FCSTD DOCUMENT  (FreeCAD 1.0R39319 (Git))
Label: assembly main
License: All rights reserved
LicenseURL: https://en.wikipedia.org/wiki/All_rights_reserved
objects: App::Link×10, App::FeaturePython×8, Assembly::AssemblyLink×2, Assembly::JointGroup×1, Assembly::AssemblyObject×1
EXTERNAL_REF file=Sub-Assembly.FCStd obj=Assembly
EXTERNAL_REF file=Sub-Assembly.FCStd obj=Base
EXTERNAL_REF file=Sub-Assembly.FCStd obj=Bracket
EXTERNAL_REF file=Sub-Assembly.FCStd obj=Bracket001
EXTERNAL_REF file=Base-Bracket.FCStd obj=Body002

FEATURE [App::Link] Base
  LinkedObject = -> <external Sub-Assembly.FCStd>#Base
FEATURE [App::Link] Bracket
  LinkPlacement = pos=(-27.5,-2.2e-15,10) rot=(0,0,1;1.5708rad)
  LinkedObject = -> <external Sub-Assembly.FCStd>#Bracket
  Placement = pos=(-27.5,-2.2e-15,10) rot=(0,0,1;1.5708rad)
FEATURE [App::Link] Bracket001
  LinkPlacement = pos=(27.5,-4.7e-15,10) rot=(0,0,-1;1.5708rad)
  LinkedObject = -> <external Sub-Assembly.FCStd>#Bracket001
  Placement = pos=(27.5,-4.7e-15,10) rot=(0,0,-1;1.5708rad)
FEATURE [Assembly::AssemblyLink] Assembly001
  Group = -> [Base,Bracket,Bracket001]
  LinkedObject = -> <external Sub-Assembly.FCStd>#Assembly
  Origin = -> Origin001
  Rigid = true
FEATURE [App::FeaturePython] GroundedJoint  # Assembly grounded joint (typed FeaturePython)
  ObjectToGround = -> Assembly001
FEATURE [App::Link] Base001
  LinkedObject = -> <external Sub-Assembly.FCStd>#Base
FEATURE [App::Link] Bracket002
  LinkPlacement = pos=(-27.5,-2.2e-15,10) rot=(0,0,1;1.5708rad)
  LinkedObject = -> <external Sub-Assembly.FCStd>#Bracket
  Placement = pos=(-27.5,-2.2e-15,10) rot=(0,0,1;1.5708rad)
FEATURE [App::Link] Bracket003
  LinkPlacement = pos=(27.5,-4.7e-15,10) rot=(0,0,-1;1.5708rad)
  LinkedObject = -> <external Sub-Assembly.FCStd>#Bracket001
  Placement = pos=(27.5,-4.7e-15,10) rot=(0,0,-1;1.5708rad)
FEATURE [Assembly::AssemblyLink] Assembly002
  Group = -> [Base001,Bracket002,Bracket003]
  LinkedObject = -> <external Sub-Assembly.FCStd>#Assembly
  Origin = -> Origin002
  Placement = pos=(-5e-16,111.569,4.2e-15) rot=(0,0,1;0rad)
  Rigid = true
FEATURE [App::FeaturePython] Joint  label="Slider"  # Assembly joint (typed FeaturePython)
  Activated = true
  AngleMax = 0
  AngleMin = 0
  Detach1 = false
  Detach2 = false
  Distance = 0
  Distance2 = 0
  EnableAngleMax = false
  EnableAngleMin = false
  EnableLengthMax = true
  EnableLengthMin = true
  JointType = 3 (Slider)
  LengthMax = 180
  LengthMin = 70
  Placement1 = pos=(-27.5,0,10) rot=(-0.57735,-0.57735,0.57735;4.18879rad)
  Placement2 = pos=(-27.5,0,10) rot=(-0.57735,-0.57735,0.57735;4.18879rad)
  Reference1 = -> Assembly [Assembly002.Base001.Edge21,Assembly002.Base001.Edge21]
  Reference2 = -> Assembly [Assembly001.Base.Edge21,Assembly001.Base.Edge21]
FEATURE [App::Link] Link
  LinkPlacement = pos=(25.5,27.8923,101.497) rot=(0.425501,0.798686,0.425501;1.79371rad)
  LinkedObject = -> <external Base-Bracket.FCStd>#Body002
  Placement = pos=(25.5,27.8923,101.497) rot=(0.425501,0.798686,0.425501;1.79371rad)
FEATURE [App::Link] Link001
  LinkPlacement = pos=(-25.5,27.8923,101.497) rot=(-0.425501,0.798686,0.425501;4.48947rad)
  LinkedObject = -> <external Base-Bracket.FCStd>#Body002
  Placement = pos=(-25.5,27.8923,101.497) rot=(-0.425501,0.798686,0.425501;4.48947rad)
FEATURE [App::Link] Link002
  LinkPlacement = pos=(25.5,83.677,101.497) rot=(0.661712,0.352528,0.661712;2.46374rad)
  LinkedObject = -> <external Base-Bracket.FCStd>#Body002
  Placement = pos=(25.5,83.677,101.497) rot=(0.661712,0.352528,0.661712;2.46374rad)
FEATURE [App::Link] Link003
  LinkPlacement = pos=(-25.5,83.677,101.497) rot=(0.425501,0.798686,-0.425501;4.48947rad)
  LinkedObject = -> <external Base-Bracket.FCStd>#Body002
  Placement = pos=(-25.5,83.677,101.497) rot=(0.425501,0.798686,-0.425501;4.48947rad)
FEATURE [App::FeaturePython] Joint001  label="Revolute"  # Assembly joint (typed FeaturePython)
  Activated = true
  AngleMax = 0
  AngleMin = 0
  Detach1 = false
  Detach2 = false
  Distance = 0
  Distance2 = 0
  EnableAngleMax = false
  EnableAngleMin = false
  EnableLengthMax = false
  EnableLengthMin = false
  JointType = 1 (Revolute)
  LengthMax = 0
  LengthMin = 0
  Placement1 = pos=(2.1316e-12,-50,2) rot=(0,0,1;0rad)
  Placement2 = pos=(0,0,50) rot=(1,0,0;1.5708rad)
  Reference1 = -> Assembly [Link002.Pad003.Edge15,Link002.Pad003.Edge15]
  Reference2 = -> Assembly [Assembly002.Bracket003.Pad002.Edge37,Assembly002.Bracket003.Pad002.Edge37]
FEATURE [App::FeaturePython] Joint002  label="Revolute001"  # Assembly joint (typed FeaturePython)
  Activated = true
  AngleMax = 0
  AngleMin = 0
  Detach1 = false
  Detach2 = false
  Distance = 0
  Distance2 = 0
  EnableAngleMax = false
  EnableAngleMin = false
  EnableLengthMax = false
  EnableLengthMin = false
  JointType = 1 (Revolute)
  LengthMax = 0
  LengthMin = 0
  Offset2 = pos=(0,0,5) rot=(0,0,1;0rad)
  Placement1 = pos=(2.1316e-12,50,2) rot=(0,0,1;0rad)
  Placement2 = pos=(-3e-16,-9e-16,50) rot=(1,0,0;1.5708rad)
  Reference1 = -> Assembly [Link003.Pad003.Edge18,Link003.Pad003.Edge18]
  Reference2 = -> Assembly [Assembly002.Bracket002.Pad002.Edge32,Assembly002.Bracket002.Pad002.Edge32]
FEATURE [App::FeaturePython] Joint003  label="Revolute002"  # Assembly joint (typed FeaturePython)
  Activated = true
  AngleMax = 0
  AngleMin = 0
  Detach1 = false
  Detach2 = false
  Distance = 0
  Distance2 = 0
  EnableAngleMax = false
  EnableAngleMin = false
  EnableLengthMax = false
  EnableLengthMin = false
  JointType = 1 (Revolute)
  LengthMax = 0
  LengthMin = 0
  Placement1 = pos=(2.1316e-12,-50,2) rot=(0,0,1;0rad)
  Placement2 = pos=(0,0,50) rot=(1,0,0;1.5708rad)
  Reference1 = -> Assembly [Link.Pad003.Edge15,Link.Pad003.Edge15]
  Reference2 = -> Assembly [Assembly001.Bracket001.Pad002.Edge37,Assembly001.Bracket001.Pad002.Edge37]
FEATURE [App::FeaturePython] Joint004  label="Revolute003"  # Assembly joint (typed FeaturePython)
  Activated = true
  AngleMax = 0
  AngleMin = 0
  Detach1 = false
  Detach2 = false
  Distance = 0
  Distance2 = 0
  EnableAngleMax = false
  EnableAngleMin = false
  EnableLengthMax = false
  EnableLengthMin = false
  JointType = 1 (Revolute)
  LengthMax = 0
  LengthMin = 0
  Placement1 = pos=(2.1316e-12,-50,2) rot=(0,0,1;0rad)
  Placement2 = pos=(0,0,50) rot=(1,0,0;1.5708rad)
  Reference1 = -> Assembly [Link001.Pad003.Edge15,Link001.Pad003.Edge15]
  Reference2 = -> Assembly [Assembly001.Bracket.Pad002.Edge37,Assembly001.Bracket.Pad002.Edge37]
FEATURE [App::FeaturePython] Joint005  label="Revolute004"  # Assembly joint (typed FeaturePython)
  Activated = true
  AngleMax = 0
  AngleMin = 0
  Detach1 = false
  Detach2 = false
  Distance = 0
  Distance2 = 0
  EnableAngleMax = false
  EnableAngleMin = false
  EnableLengthMax = false
  EnableLengthMin = false
  JointType = 1 (Revolute)
  LengthMax = 0
  LengthMin = 0
  Placement1 = pos=(2.1316e-12,-50,1) rot=(0,0,1;0rad)
  Placement2 = pos=(2.1316e-12,50,1) rot=(0,0,1;0rad)
  Reference1 = -> Assembly [Link003.Pad003.Face5,Link003.Pad003.Face5]
  Reference2 = -> Assembly [Link001.Pad003.Face6,Link001.Pad003.Face6]
FEATURE [App::FeaturePython] Joint006  label="Revolute005"  # Assembly joint (typed FeaturePython)
  Activated = true
  AngleMax = 0
  AngleMin = 0
  Detach1 = false
  Detach2 = false
  Distance = 0
  Distance2 = 0
  EnableAngleMax = false
  EnableAngleMin = false
  EnableLengthMax = false
  EnableLengthMin = false
  JointType = 1 (Revolute)
  LengthMax = 0
  LengthMin = 0
  Placement1 = pos=(2.1174e-12,50,1) rot=(0,0,1;0rad)
  Placement2 = pos=(2.1174e-12,50,1) rot=(0,0,1;0rad)
  Reference1 = -> Assembly [Link002.Pad003.Face6,Link002.Pad003.Face6]
  Reference2 = -> Assembly [Link.Pad003.Face6,Link.Pad003.Face6]
FEATURE [Assembly::JointGroup] Joints
  Group = -> [GroundedJoint,Joint,Joint001,Joint002,Joint003,Joint004,Joint005,Joint006]
FEATURE [Assembly::AssemblyObject] Assembly
  Group = -> [Joints,Assembly001,GroundedJoint,Assembly002,Joint,Link,Link001,Link002,Link003,Joint001,Joint002,Joint003,Joint004,Joint005,Joint006]
  Origin = -> Origin
  Type = Assembly

RESOLVED EXTERNAL PARTS (link-assembly join: the EXTERNAL_REF files above that resolve inside this repo's crawl, each included once):
---- part Base-Bracket.FCStd = doc fcstd_38e4ad80bfca ----
FCSTD DOCUMENT  (FreeCAD 1.0R39319 (Git))
Label: Base-Bracket
License: All rights reserved
LicenseURL: https://en.wikipedia.org/wiki/All_rights_reserved
objects: Sketcher::SketchObject×5, PartDesign::Pad×4, PartDesign::Body×3, PartDesign::Pocket×1
note: 28 computed .brp shape members not serialized (recipe doc carries the construction recipe); baked Part::Feature solids carry a one-line shape summary decoded from their .brp

FEATURE [Sketcher::SketchObject] Sketch
  ArcFitTolerance = 1e-06
  AttachmentSupport = -> [XY_Plane]
  FullyConstrained = true
  MakeInternals = false
  MapMode = 5
  sketch-geometry (14):
    g0: LineSegment StartX=-52.5 StartY=13 StartZ=0 EndX=-52.5 EndY=-13 EndZ=0
    g1: LineSegment StartX=-40.5 StartY=-25 StartZ=0 EndX=40.5 EndY=-25 EndZ=0
    g2: LineSegment StartX=52.5 StartY=-13 StartZ=0 EndX=52.5 EndY=13 EndZ=0
    g3: LineSegment StartX=40.5 StartY=25 StartZ=0 EndX=-40.5 EndY=25 EndZ=0
    g4: ArcOfCircle CenterX=-40.5 CenterY=13 CenterZ=0 NormalX=0 NormalY=0 NormalZ=1 AngleXU=0 Radius=12 StartAngle=1.5708 EndAngle=3.14159
    g5: ArcOfCircle CenterX=-40.5 CenterY=-13 CenterZ=0 NormalX=0 NormalY=0 NormalZ=1 AngleXU=0 Radius=12 StartAngle=3.14159 EndAngle=4.71239
    g6: ArcOfCircle CenterX=40.5 CenterY=-13 CenterZ=0 NormalX=0 NormalY=0 NormalZ=1 AngleXU=0 Radius=12 StartAngle=4.71239 EndAngle=6.28319
    g7: ArcOfCircle CenterX=40.5 CenterY=13 CenterZ=0 NormalX=0 NormalY=0 NormalZ=1 AngleXU=0 Radius=12 StartAngle=0 EndAngle=1.5708
    g8: GeomPoint [constr] X=-52.5 Y=25 Z=0
    g9: GeomPoint [constr] X=52.5 Y=-25 Z=0
    g10: Circle CenterX=-40.5 CenterY=13 CenterZ=0 NormalX=0 NormalY=0 NormalZ=1 AngleXU=0 Radius=4
    g11: Circle CenterX=-40.5 CenterY=-13 CenterZ=0 NormalX=0 NormalY=0 NormalZ=1 AngleXU=0 Radius=4
    g12: Circle CenterX=40.5 CenterY=13 CenterZ=0 NormalX=0 NormalY=0 NormalZ=1 AngleXU=0 Radius=4
    g13: Circle CenterX=40.5 CenterY=-13 CenterZ=0 NormalX=0 NormalY=0 NormalZ=1 AngleXU=0 Radius=4
  constraints (31):
    c: Tangent(g0,g4) = -1.5708
    c: Tangent(g0,g5) = -1.5708
    c: Tangent(g1,g5) = -1.5708
    c: Tangent(g1,g6) = -1.5708
    c: Tangent(g2,g6) = -1.5708
    c: Tangent(g2,g7) = -1.5708
    c: Tangent(g3,g7) = -1.5708
    c: Tangent(g3,g4) = -1.5708
    c: Vertical(g0)
    c: Vertical(g2)
    c: Horizontal(g1)
    c: Horizontal(g3)
    c: Equal(g4,g5)
    c: Equal(g5,g6)
    c: Equal(g6,g7)
    c: PointOnObject(g8,g0)
    c: PointOnObject(g8,g3)
    c: PointOnObject(g9,g1)
    c: PointOnObject(g9,g2)
    c: Symmetric(g4,g6,g-1)
    c: Distance(g1,g3) = 50
    c: Radius(g7) = 12
    c: Distance(g2,g0) = 105
    c: Diameter(g10) = 8
    c: Coincident(g10,g4)
    c: Diameter(g11) = 8
    c: Block(g11)
    c: Diameter(g12) = 8
    c: Diameter(g13) = 8
    c: Block(g13)
    c: Block(g12)
FEATURE [PartDesign::Pad] Pad
  Direction = (0,0,1)
  Length = 10
  Length2 = 10
  Profile = -> Sketch
  ReferenceAxis = -> Sketch [N_Axis]
  Refine = true
  Suppressed = false
  Type = 0
FEATURE [Sketcher::SketchObject] Sketch001
  ArcFitTolerance = 1e-06
  AttachmentSupport = -> [Pad]
  ExternalGeometry = -> [Pad]
  FullyConstrained = true
  MakeInternals = false
  MapMode = 5
  Placement = pos=(0,0,10) rot=(0,0,1;0rad)
  sketch-geometry (4):
    g0: LineSegment StartX=-27.5 StartY=25 StartZ=0 EndX=-27.5 EndY=-25 EndZ=0
    g1: LineSegment StartX=-27.5 StartY=-25 StartZ=0 EndX=27.5 EndY=-25 EndZ=0
    g2: LineSegment StartX=27.5 StartY=-25 StartZ=0 EndX=27.5 EndY=25 EndZ=0
    g3: LineSegment StartX=27.5 StartY=25 StartZ=0 EndX=-27.5 EndY=25 EndZ=0
  constraints (11):
    c: Coincident(g0,g1)
    c: Coincident(g1,g2)
    c: Coincident(g2,g3)
    c: Coincident(g3,g0)
    c: Vertical(g0)
    c: Vertical(g2)
    c: Horizontal(g1)
    c: Horizontal(g3)
    c: Symmetric(g0,g1,g-1)
    c: PointOnObject(g0,g-3)
    c: Distance(g2,g0) = 55
FEATURE [PartDesign::Pocket] Pocket
  BaseFeature = -> Pad
  Direction = (0,0,-1)
  Length = 5
  Length2 = 5
  Profile = -> Sketch001
  ReferenceAxis = -> Sketch001 [N_Axis]
  Refine = true
  Suppressed = false
  Type = 0
FEATURE [PartDesign::Body] Body  label="Base"
  AllowCompound = false
  Group = -> [Sketch,Pad,Sketch001,Pocket]
  Origin = -> Origin
  Tip = -> Pocket
FEATURE [Sketcher::SketchObject] Sketch002
  ArcFitTolerance = 1e-06
  AttachmentSupport = -> [XY_Plane001]
  FullyConstrained = true
  MakeInternals = false
  MapMode = 5
  sketch-geometry (10):
    g0: LineSegment StartX=-25 StartY=13 StartZ=0 EndX=-25 EndY=0 EndZ=0
    g1: LineSegment StartX=-25 StartY=0 StartZ=0 EndX=25 EndY=0 EndZ=0
    g2: LineSegment StartX=25 StartY=0 StartZ=0 EndX=25 EndY=13 EndZ=0
    g3: LineSegment StartX=13 StartY=25 StartZ=0 EndX=-13 EndY=25 EndZ=0
    g4: ArcOfCircle CenterX=-13 CenterY=13 CenterZ=0 NormalX=0 NormalY=0 NormalZ=1 AngleXU=0 Radius=12 StartAngle=1.5708 EndAngle=3.14159
    g5: GeomPoint [constr] X=-25 Y=25 Z=0
    g6: ArcOfCircle CenterX=13 CenterY=13 CenterZ=0 NormalX=0 NormalY=0 NormalZ=1 AngleXU=0 Radius=12 StartAngle=0 EndAngle=1.5708
    g7: GeomPoint [constr] X=25 Y=25 Z=0
    g8: Circle CenterX=13 CenterY=13 CenterZ=0 NormalX=0 NormalY=0 NormalZ=1 AngleXU=0 Radius=4
    g9: Circle CenterX=-13 CenterY=13 CenterZ=0 NormalX=0 NormalY=0 NormalZ=1 AngleXU=0 Radius=4
  constraints (23):
    c: Coincident(g0,g1)
    c: Coincident(g1,g2)
    c: Vertical(g0)
    c: Vertical(g2)
    c: Horizontal(g1)
    c: Horizontal(g3)
    c: PointOnObject(g1,g-1)
    c: PointOnObject(g5,g0)
    c: PointOnObject(g5,g3)
    c: Tangent(g0,g4) = -1.5708
    c: Tangent(g3,g4) = -1.5708
    c: PointOnObject(g7,g3)
    c: PointOnObject(g7,g2)
    c: Tangent(g3,g6) = -1.5708
    c: Tangent(g2,g6) = -1.5708
    c: Distance(g2,g0) = 50
    c: Distance(g1,g3) = 25
    c: Radius(g6) = 12
    c: Symmetric(g4,g6,g-2)
    c: Diameter(g8) = 8
    c: Coincident(g8,g6)
    c: Diameter(g9) = 8
    c: Block(g9)
FEATURE [PartDesign::Pad] Pad001
  Direction = (0,0,1)
  Length = 10
  Length2 = 10
  Profile = -> Sketch002
  ReferenceAxis = -> Sketch002 [N_Axis]
  Refine = true
  Suppressed = false
  Type = 0
FEATURE [Sketcher::SketchObject] Sketch003
  ArcFitTolerance = 1e-06
  AttachmentSupport = -> [Pad001]
  ExternalGeometry = -> [Pad001]
  FullyConstrained = true
  MakeInternals = false
  MapMode = 5
  Placement = pos=(0,0,0) rot=(1,0,0;1.5708rad)
  sketch-geometry (5):
    g0: ArcOfCircle CenterX=-63.5588 CenterY=50 CenterZ=0 NormalX=0 NormalY=0 NormalZ=1 AngleXU=0 Radius=55.5588 StartAngle=5.47944 EndAngle=6.28319
    g1: ArcOfCircle CenterX=0 CenterY=50 CenterZ=0 NormalX=0 NormalY=0 NormalZ=1 AngleXU=0 Radius=8 StartAngle=0 EndAngle=3.14159
    g2: ArcOfCircle CenterX=63.5588 CenterY=50 CenterZ=0 NormalX=0 NormalY=0 NormalZ=1 AngleXU=0 Radius=55.5588 StartAngle=3.14159 EndAngle=3.94533
    g3: Circle CenterX=0 CenterY=50 CenterZ=0 NormalX=0 NormalY=0 NormalZ=1 AngleXU=0 Radius=2.5
    g4: LineSegment StartX=-25 StartY=10 StartZ=0 EndX=25 EndY=10 EndZ=0
  constraints (13):
    c: Tangent(g0,g1) = 1.5708
    c: Tangent(g1,g2) = 1.5708
    c: Coincident(g2,g-3)
    c: Coincident(g-3,g0)
    c: Horizontal(g0,g1)
    c: PointOnObject(g1,g-2)
    c: Horizontal(g0,g1)
    c: DistanceY(g-1,g1) = 50
    c: Radius(g1) = 8
    c: Diameter(g3) = 5
    c: Coincident(g3,g1)
    c: Coincident(g4,g0)
    c: Coincident(g4,g2)
FEATURE [PartDesign::Pad] Pad002
  BaseFeature = -> Pad001
  Direction = (0,-1,2e-16)
  Length = 5
  Length2 = 10
  Profile = -> Sketch003
  ReferenceAxis = -> Sketch003 [N_Axis]
  Refine = true
  Reversed = true
  Suppressed = false
  Type = 0
FEATURE [PartDesign::Body] Body001  label="Bracket"
  AllowCompound = false
  Group = -> [Sketch002,Pad001,Sketch003,Pad002]
  Origin = -> Origin001
  Placement = pos=(26.0989,2.26605,52) rot=(0,0,-1;2.96706rad)
  Tip = -> Pad002
FEATURE [Sketcher::SketchObject] Sketch004
  ArcFitTolerance = 1e-06
  AttachmentSupport = -> [XY_Plane002]
  FullyConstrained = true
  MakeInternals = false
  MapMode = 5
  sketch-geometry (6):
    g0: ArcOfCircle CenterX=2.1316e-12 CenterY=50 CenterZ=0 NormalX=0 NormalY=0 NormalZ=1 AngleXU=0 Radius=8 StartAngle=-2.24e-12 EndAngle=3.14159
    g1: ArcOfCircle CenterX=-2.1314e-12 CenterY=-50 CenterZ=0 NormalX=0 NormalY=0 NormalZ=1 AngleXU=0 Radius=8 StartAngle=3.14159 EndAngle=6.28319
    g2: LineSegment StartX=8 StartY=50 StartZ=0 EndX=8 EndY=-50 EndZ=0
    g3: LineSegment StartX=-8 StartY=50 StartZ=0 EndX=-8 EndY=-50 EndZ=0
    g4: Circle CenterX=2.1316e-12 CenterY=50 CenterZ=0 NormalX=0 NormalY=0 NormalZ=1 AngleXU=0 Radius=2.5
    g5: Circle CenterX=2.1316e-12 CenterY=-50 CenterZ=0 NormalX=0 NormalY=0 NormalZ=1 AngleXU=0 Radius=2.5
  constraints (13):
    c: Tangent(g0,g2) = 1.5708
    c: Tangent(g0,g3) = -1.5708
    c: Tangent(g1,g2) = 1.5708
    c: Tangent(g1,g3) = -1.5708
    c: Equal(g0,g1)
    c: Vertical(g3)
    c: Coincident(g4,g0)
    c: Diameter(g4) = 5
    c: Radius(g0) = 8
    c: Symmetric(g0,g1,g-1)
    c: DistanceY(g-1,g0) = 50
    c: Diameter(g5) = 5
    c: Block(g5)
FEATURE [PartDesign::Pad] Pad003
  Direction = (0,0,1)
  Length = 2
  Length2 = 10
  Profile = -> Sketch004
  ReferenceAxis = -> Sketch004 [N_Axis]
  Refine = true
  Suppressed = false
  Type = 0
FEATURE [PartDesign::Body] Body002  label="Link"
  AllowCompound = false
  Group = -> [Sketch004,Pad003]
  Origin = -> Origin002
  Placement = pos=(-39,0,52) rot=(0,0,1;0rad)
  Tip = -> Pad003
---- part Sub-Assembly.FCStd = doc fcstd_82f28e0bf703 ----
FCSTD DOCUMENT  (FreeCAD 1.0R39319 (Git))
Label: Sub-Assembly
License: All rights reserved
LicenseURL: https://en.wikipedia.org/wiki/All_rights_reserved
objects: App::Link×3, App::FeaturePython×3, Assembly::JointGroup×1, Assembly::AssemblyObject×1
EXTERNAL_REF file=Base-Bracket.FCStd obj=Body
EXTERNAL_REF file=Base-Bracket.FCStd obj=Body001

FEATURE [App::Link] Base
  LinkedObject = -> <external Base-Bracket.FCStd>#Body
FEATURE [App::FeaturePython] GroundedJoint  # Assembly grounded joint (typed FeaturePython)
  ObjectToGround = -> Base
FEATURE [App::Link] Bracket
  LinkPlacement = pos=(-27.5,-2.2e-15,10) rot=(0,0,1;1.5708rad)
  LinkedObject = -> <external Base-Bracket.FCStd>#Body001
  Placement = pos=(-27.5,-2.2e-15,10) rot=(0,0,1;1.5708rad)
FEATURE [App::Link] Bracket001
  LinkPlacement = pos=(27.5,-4.7e-15,10) rot=(0,0,-1;1.5708rad)
  LinkedObject = -> <external Base-Bracket.FCStd>#Body001
  Placement = pos=(27.5,-4.7e-15,10) rot=(0,0,-1;1.5708rad)
FEATURE [App::FeaturePython] Joint  label="Fixed"  # Assembly joint (typed FeaturePython)
  Activated = true
  AngleMax = 0
  AngleMin = 0
  Detach1 = false
  Detach2 = false
  Distance = 0
  Distance2 = 0
  EnableAngleMax = false
  EnableAngleMin = false
  EnableLengthMax = false
  EnableLengthMin = false
  JointType = 0 (Fixed)
  LengthMax = 0
  LengthMin = 0
  Offset2 = pos=(0,0,10) rot=(0,0,1;1.5708rad)
  Placement1 = pos=(13,13,10) rot=(0,0,1;0rad)
  Placement2 = pos=(-40.5,13,20) rot=(0,0,1;1.5708rad)
  Reference1 = -> Assembly [Bracket.Edge20,Bracket.Edge20]
  Reference2 = -> Assembly [Base.Edge24,Base.Edge24]
FEATURE [App::FeaturePython] Joint001  label="Fixed001"  # Assembly joint (typed FeaturePython)
  Activated = true
  AngleMax = 0
  AngleMin = 0
  Detach1 = false
  Detach2 = false
  Distance = 0
  Distance2 = 0
  EnableAngleMax = false
  EnableAngleMin = false
  EnableLengthMax = false
  EnableLengthMin = false
  JointType = 0 (Fixed)
  LengthMax = 0
  LengthMin = 0
  Offset2 = pos=(0,0,10) rot=(0,0,-1;1.5708rad)
  Placement1 = pos=(13,13,10) rot=(0,0,1;0rad)
  Placement2 = pos=(40.5,-13,20) rot=(0,0,-1;1.5708rad)
  Reference1 = -> Assembly [Bracket001.Edge20,Bracket001.Edge20]
  Reference2 = -> Assembly [Base.Edge41,Base.Edge41]
FEATURE [Assembly::JointGroup] Joints
  Group = -> [GroundedJoint,Joint,Joint001]
FEATURE [Assembly::AssemblyObject] Assembly
  Group = -> [Joints,Base,GroundedJoint,Bracket,Bracket001,Joint,Joint001]
  Origin = -> Origin
  Type = Assembly
